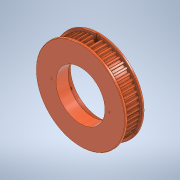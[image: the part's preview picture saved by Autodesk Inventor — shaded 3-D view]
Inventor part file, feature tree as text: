
AUTODESK INVENTOR PART (.ipt)
format: ipt  version: 2020 (Build 240168000, 168)  size: 867,328 bytes
history: native  units: mm
features: extrude x10, sketch x10, projected_geometry x5, pattern_circular x2, plane x2, fillet x1
ambient origin geometry x8: Origin, YZ Plane, XZ Plane, XY Plane, X Axis, Y Axis, Z Axis, Center Point
bodies: Solid1 (feature_tree)
feature tree (30):
  extrude  "Extrusion1"  Depth=2.0mm TaperAngle=0.0deg
  extrude  "Extrusion2"  Depth=16.5mm TaperAngle=0.0deg
  extrude  "Extrusion3"  Depth=0.27557mm
  pattern_circular  "Circular Pattern1"  Count=57 Angle=360.0deg
  extrude  "Extrusion4"  Depth=2.0mm TaperAngle=0.0deg
  extrude  "Extrusion5"  Depth=0.9mm TaperAngle=0.0deg
  extrude  "Extrusion6"  Depth=10.0mm
  extrude  "Extrusion7"  Depth=10.0mm
  extrude  "Extrusion8"  Depth=10.0mm TaperAngle=0.0deg
  plane  "Work Plane1"
  extrude  "Extrusion9"  Depth=10.0mm
  plane  "Work Plane2"
  extrude  "Extrusion12"  Depth=10.0mm TaperAngle=0.0deg
  pattern_circular  "Circular Pattern2"  [2 undecoded]
  fillet  "Fillet1"  Radius=50.0mm
  sketch  "Sketch1"  dims[d0=100.0mm d1=2.0mm d2=0.0mm]
  sketch  "Sketch2"  dims[d3=90.0mm d4=16.5mm d5=0.0mm]
  sketch  "Sketch3"  dims[d6=94.3471mm d7=0.27557mm]
  projected_geometry  "Projected Loop1"
  projected_geometry  "Projected Loop2"
  sketch  "Sketch4"  dims[d8=0.27557mm]
  sketch  "Sketch5"  dims[d9=0.4mm]
  sketch  "Sketch6"  dims[d10=0.4mm]
  sketch  "Sketch7"  dims[d11=16.0mm d12=0.0mm d13=570.0mm d14=360.0deg]
  sketch  "Sketch8"  dims[d16=100.0mm d17=2.0mm d18=0.0mm]
  sketch  "Sketch9"  dims[d19=100.0mm d20=0.9mm d21=0.0mm]
  projected_geometry  "Projected Loop3"
  projected_geometry  "Projected Loop4"
  projected_geometry  "Projected Loop5"
  sketch  "Sketch12"  dims[d22=65.0mm d23=1.0mm d24=1.0mm d25=10.0mm d26=0.0mm d27=65.6mm d28=7.9mm d29=0.0mm d30=55.0mm d31=50.0mm d32=0.0mm d33=47.75mm d35=2.5mm d36=2.1mm d37=50.0mm d38=0.0mm d42=-47.75mm d46=0.5mm d47=5.25mm d48=10.0mm d49=0.0mm d51=30.0mm d52=360.0deg d39=0.872665mm]
note: 2 required parameter values undecoded (feature->parameter linkage not recoverable at this tier; creation-order binding heuristic only, values carry confidence <= 0.55)
